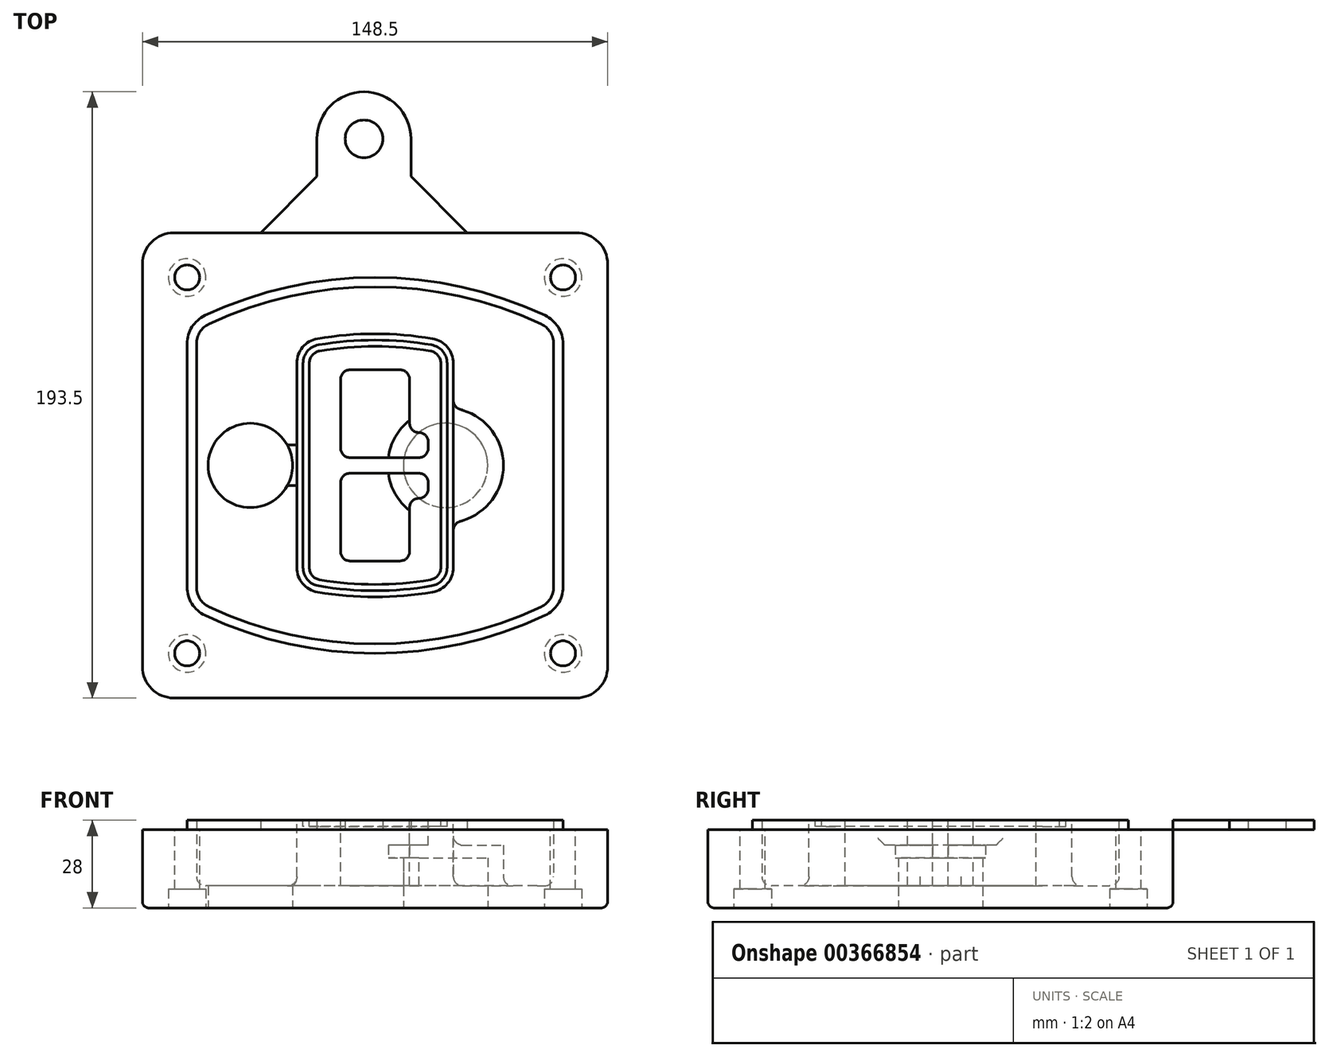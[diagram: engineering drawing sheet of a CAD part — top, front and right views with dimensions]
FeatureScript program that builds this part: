
annotation { "Feature Type Name" : "Feature", "Feature Type Description" : "" }
export const myFeature = defineFeature(function(context is Context, id is Id, definition is map)
    precondition{}
    {
        {
            var Q0;
            Q0=qCreatedBy(makeId("Top.planeOp"),FACE);
            var sketch = newSketch(context, id + "F0", { "sketchPlane" : qUnion([Q0])});
            skPoint(sketch, "E0.rect.middle", {"position": v(0, 0) * mm});
            skLineSegment(sketch, "E1.bottom", {"start": v(-64.25, -74.25) * mm, "end": v(64.25, -74.25) * mm});
            skLineSegment(sketch, "E1.top", {"start": v(-64.25, 74.25) * mm, "end": v(64.25, 74.25) * mm});
            skLineSegment(sketch, "E1.left", {"start": v(-74.25, -64.25) * mm, "end": v(-74.25, 64.25) * mm});
            skLineSegment(sketch, "E1.right", {"start": v(74.25, -64.25) * mm, "end": v(74.25, 64.25) * mm});
            skLineSegment(sketch, "E2", {"start": v(-74.25, 74.25) * mm, "end": v(74.25, -74.25) * mm, "construction": true});
            skLineSegment(sketch, "E3", {"start": v(74.25, 74.25) * mm, "end": v(-74.25, -74.25) * mm, "construction": true});
            skCircle(sketch, "E4", {"center": v(-60, 60) * mm, "radius": 4 * mm});
            skCircle(sketch, "E5", {"center": v(60, 60) * mm, "radius": 4 * mm});
            skCircle(sketch, "E6", {"center": v(60, -60) * mm, "radius": 4 * mm});
            skCircle(sketch, "E7", {"center": v(-60, -60) * mm, "radius": 4 * mm});
            skLineSegment(sketch, "E8", {"start": v(-60, 60) * mm, "end": v(60, 60) * mm, "construction": true});
            skLineSegment(sketch, "E9", {"start": v(60, 60) * mm, "end": v(60, -60) * mm, "construction": true});
            skLineSegment(sketch, "E10", {"start": v(60, -60) * mm, "end": v(-60, -60) * mm, "construction": true});
            skLineSegment(sketch, "E11", {"start": v(-60, -60) * mm, "end": v(-60, 60) * mm, "construction": true});
            skLineSegment(sketch, "E12", {"start": v(-60, 38.83) * mm, "end": v(-60, -38.83) * mm});
            skLineSegment(sketch, "E13", {"start": v(60, 38.83) * mm, "end": v(60, -38.83) * mm});
            skArc(sketch, "E14", {"start": v(54.26, 47.88) * mm, "mid": v(0, 60) * mm, "end": v(-54.26, 47.88) * mm});
            skArc(sketch, "E15", {"start": v(-54.26, -47.88) * mm, "mid": v(0, -60) * mm, "end": v(54.26, -47.88) * mm});
            skLineSegment(sketch, "E16", {"start": v(-60, 0) * mm, "end": v(60, 0) * mm, "construction": true});
            skPoint(sketch, "E17.visualSharp", {"position": v(-60, -45) * mm});
            skArc(sketch, "E17.filletArc", {"start": v(-60, -38.83) * mm, "mid": v(-58.44, -44.2) * mm, "end": v(-54.26, -47.88) * mm});
            skPoint(sketch, "E18.visualSharp", {"position": v(-60, 45) * mm});
            skArc(sketch, "E18.filletArc", {"start": v(-54.26, 47.88) * mm, "mid": v(-58.44, 44.2) * mm, "end": v(-60, 38.83) * mm});
            skPoint(sketch, "E19.visualSharp", {"position": v(60, 45) * mm});
            skArc(sketch, "E19.filletArc", {"start": v(60, 38.83) * mm, "mid": v(58.44, 44.2) * mm, "end": v(54.26, 47.88) * mm});
            skPoint(sketch, "E20.visualSharp", {"position": v(60, -45) * mm});
            skArc(sketch, "E20.filletArc", {"start": v(54.26, -47.88) * mm, "mid": v(58.44, -44.2) * mm, "end": v(60, -38.83) * mm});
            skPoint(sketch, "E21.visualSharp", {"position": v(-74.25, 74.25) * mm});
            skArc(sketch, "E21.filletArc", {"start": v(-64.25, 74.25) * mm, "mid": v(-71.32, 71.32) * mm, "end": v(-74.25, 64.25) * mm});
            skPoint(sketch, "E22.visualSharp", {"position": v(74.25, 74.25) * mm});
            skArc(sketch, "E22.filletArc", {"start": v(74.25, 64.25) * mm, "mid": v(71.32, 71.32) * mm, "end": v(64.25, 74.25) * mm});
            skPoint(sketch, "E23.visualSharp", {"position": v(74.25, -74.25) * mm});
            skArc(sketch, "E23.filletArc", {"start": v(64.25, -74.25) * mm, "mid": v(71.32, -71.32) * mm, "end": v(74.25, -64.25) * mm});
            skPoint(sketch, "E24.visualSharp", {"position": v(-74.25, -74.25) * mm});
            skArc(sketch, "E24.filletArc", {"start": v(-74.25, -64.25) * mm, "mid": v(-71.32, -71.32) * mm, "end": v(-64.25, -74.25) * mm});
            skArc(sketch, "E25.0", {"start": v(57, 38.83) * mm, "mid": v(55.9, 42.58) * mm, "end": v(52.98, 45.17) * mm});
            skLineSegment(sketch, "E25.1", {"start": v(57, 38.83) * mm, "end": v(57, -38.83) * mm});
            skArc(sketch, "E25.2", {"start": v(52.98, -45.17) * mm, "mid": v(55.9, -42.58) * mm, "end": v(57, -38.83) * mm});
            skArc(sketch, "E25.3", {"start": v(-52.98, -45.17) * mm, "mid": v(0, -57) * mm, "end": v(52.98, -45.17) * mm});
            skArc(sketch, "E25.4", {"start": v(-57, -38.83) * mm, "mid": v(-55.9, -42.58) * mm, "end": v(-52.98, -45.17) * mm});
            skArc(sketch, "E25.5", {"start": v(52.98, 45.17) * mm, "mid": v(0, 57) * mm, "end": v(-52.98, 45.17) * mm});
            skLineSegment(sketch, "E25.6", {"start": v(-57, 38.83) * mm, "end": v(-57, -38.83) * mm});
            skArc(sketch, "E25.7", {"start": v(-52.98, 45.17) * mm, "mid": v(-55.9, 42.58) * mm, "end": v(-57, 38.83) * mm});
            skArc(sketch, "E26.0", {"start": v(-55.96, 51.5) * mm, "mid": v(-61.82, 46.33) * mm, "end": v(-64, 38.83) * mm});
            skArc(sketch, "E26.1", {"start": v(55.96, 51.5) * mm, "mid": v(0, 64) * mm, "end": v(-55.96, 51.5) * mm});
            skArc(sketch, "E26.2", {"start": v(64, 38.83) * mm, "mid": v(61.82, 46.33) * mm, "end": v(55.96, 51.5) * mm});
            skLineSegment(sketch, "E26.3", {"start": v(64, 38.83) * mm, "end": v(64, -38.83) * mm});
            skArc(sketch, "E26.4", {"start": v(55.96, -51.5) * mm, "mid": v(61.82, -46.33) * mm, "end": v(64, -38.83) * mm});
            skLineSegment(sketch, "E26.5", {"start": v(-64, 38.83) * mm, "end": v(-64, -38.83) * mm});
            skArc(sketch, "E26.6", {"start": v(-55.96, -51.5) * mm, "mid": v(0, -64) * mm, "end": v(55.96, -51.5) * mm});
            skArc(sketch, "E26.7", {"start": v(-64, -38.83) * mm, "mid": v(-61.82, -46.33) * mm, "end": v(-55.96, -51.5) * mm});
            skSolve(sketch);
        }
        {
            var Q0;
            Q0=makeQuery(id+"F0.imprint","IMPRINT",FACE,{"disambiguationData":[TD([[makeQuery(id+"F0.imprint","IMPRINT",EDGE,{"derivedFrom":sQuery(id+"F0.wireOp",EDGE,"E1.bottom")}),1.0]])]});
            var Q1;
            Q1=makeQuery(id+"F0.imprint","IMPRINT",FACE,{"disambiguationData":[TD([[makeQuery(id+"F0.imprint","IMPRINT",EDGE,{"derivedFrom":sQuery(id+"F0.wireOp",EDGE,"E12")}),1.0]])]});
            var Q2;
            Q2=makeQuery(id+"F0.imprint","IMPRINT",FACE,{"disambiguationData":[TD([[makeQuery(id+"F0.imprint","IMPRINT",EDGE,{"derivedFrom":sQuery(id+"F0.wireOp",EDGE,"E25.0")}),1.0]])]});
            var Q3;
            Q3=makeQuery(id+"F0.imprint","IMPRINT",FACE,{"disambiguationData":[TD([[makeQuery(id+"F0.imprint","IMPRINT",EDGE,{"derivedFrom":sQuery(id+"F0.wireOp",EDGE,"E12")}),-1.0]])]});
            extrude(context, id + "F1", {"entities" : qUnion([Q0, Q1, Q2, Q3]), "oppositeDirection" : true, "depth" : 25 * mm});
        }
        {
            var Q0;
            Q0=makeQuery(id+"F0.imprint","IMPRINT",FACE,{"disambiguationData":[TD([[makeQuery(id+"F0.imprint","IMPRINT",EDGE,{"derivedFrom":sQuery(id+"F0.wireOp",EDGE,"E12")}),1.0]])]});
            extrude(context, id + "F2", {"entities" : qUnion([Q0]), "operationType" : NewBodyOperationType.ADD, "depth" : 3 * mm});
        }
        {
            var Q0;
            Q0=makeQuery(id+"F0.imprint","IMPRINT",FACE,{"disambiguationData":[TD([[makeQuery(id+"F0.imprint","IMPRINT",EDGE,{"derivedFrom":sQuery(id+"F0.wireOp",EDGE,"E25.0")}),1.0]])]});
            extrude(context, id + "F3", {"entities" : qUnion([Q0]), "operationType" : NewBodyOperationType.REMOVE, "oppositeDirection" : true, "depth" : 18 * mm});
        }
        {
            var Q0;
            Q0=makeQuery(id+"F2.opExtrude","CAP_FACE",FACE,{"disambiguationData":[OSD([sQuery(id+"F0.wireOp",EDGE,"E12"),sQuery(id+"F0.wireOp",EDGE,"E13"),sQuery(id+"F0.wireOp",EDGE,"E14"),sQuery(id+"F0.wireOp",EDGE,"E15"),sQuery(id+"F0.wireOp",EDGE,"E17.filletArc"),sQuery(id+"F0.wireOp",EDGE,"E18.filletArc"),sQuery(id+"F0.wireOp",EDGE,"E19.filletArc"),sQuery(id+"F0.wireOp",EDGE,"E20.filletArc"),sQuery(id+"F0.wireOp",EDGE,"E25.0"),sQuery(id+"F0.wireOp",EDGE,"E25.1"),sQuery(id+"F0.wireOp",EDGE,"E25.2"),sQuery(id+"F0.wireOp",EDGE,"E25.3"),sQuery(id+"F0.wireOp",EDGE,"E25.4"),sQuery(id+"F0.wireOp",EDGE,"E25.5"),sQuery(id+"F0.wireOp",EDGE,"E25.6"),sQuery(id+"F0.wireOp",EDGE,"E25.7")])],"isStart":false});
            var sketch = newSketch(context, id + "F4", { "sketchPlane" : qUnion([Q0])});
            skArc(sketch, "E27.0", {"start": v(-18.34, -40.45) * mm, "mid": v(0, -42) * mm, "end": v(18.34, -40.45) * mm});
            skArc(sketch, "E28.0", {"start": v(18.34, 40.45) * mm, "mid": v(0, 42) * mm, "end": v(-18.34, 40.45) * mm});
            skLineSegment(sketch, "E29", {"start": v(-25, 32.57) * mm, "end": v(-25, -32.57) * mm});
            skLineSegment(sketch, "E30", {"start": v(25, 32.57) * mm, "end": v(25, -32.57) * mm});
            skLineSegment(sketch, "E31", {"start": v(-25, 39.1) * mm, "end": v(25, 39.1) * mm, "construction": true});
            skLineSegment(sketch, "E32", {"start": v(-25, -39.1) * mm, "end": v(25, -39.1) * mm, "construction": true});
            skPoint(sketch, "E33.visualSharp", {"position": v(-25, 39.1) * mm});
            skArc(sketch, "E33.filletArc", {"start": v(-18.34, 40.45) * mm, "mid": v(-23.11, 37.73) * mm, "end": v(-25, 32.57) * mm});
            skPoint(sketch, "E34.visualSharp", {"position": v(25, 39.1) * mm});
            skArc(sketch, "E34.filletArc", {"start": v(25, 32.57) * mm, "mid": v(23.11, 37.73) * mm, "end": v(18.34, 40.45) * mm});
            skPoint(sketch, "E35.visualSharp", {"position": v(25, -39.1) * mm});
            skArc(sketch, "E35.filletArc", {"start": v(18.34, -40.45) * mm, "mid": v(23.11, -37.73) * mm, "end": v(25, -32.57) * mm});
            skPoint(sketch, "E36.visualSharp", {"position": v(-25, -39.1) * mm});
            skArc(sketch, "E36.filletArc", {"start": v(-25, -32.57) * mm, "mid": v(-23.11, -37.73) * mm, "end": v(-18.34, -40.45) * mm});
            skArc(sketch, "E37.0", {"start": v(52.98, 45.17) * mm, "mid": v(0, 57) * mm, "end": v(-52.98, 45.17) * mm});
            skArc(sketch, "E37.1", {"start": v(-52.98, 45.17) * mm, "mid": v(-55.9, 42.58) * mm, "end": v(-57, 38.83) * mm});
            skLineSegment(sketch, "E37.2", {"start": v(-57, 38.83) * mm, "end": v(-57, -38.83) * mm});
            skArc(sketch, "E37.3", {"start": v(-57, -38.83) * mm, "mid": v(-55.9, -42.58) * mm, "end": v(-52.98, -45.17) * mm});
            skArc(sketch, "E37.4", {"start": v(-52.98, -45.17) * mm, "mid": v(0, -57) * mm, "end": v(52.98, -45.17) * mm});
            skArc(sketch, "E37.5", {"start": v(52.98, -45.17) * mm, "mid": v(55.9, -42.58) * mm, "end": v(57, -38.83) * mm});
            skLineSegment(sketch, "E37.6", {"start": v(57, 38.83) * mm, "end": v(57, -38.83) * mm});
            skArc(sketch, "E37.7", {"start": v(57, 38.83) * mm, "mid": v(55.9, 42.58) * mm, "end": v(52.98, 45.17) * mm});
            skLineSegment(sketch, "E38.0", {"start": v(23, 32.57) * mm, "end": v(23, -32.57) * mm});
            skArc(sketch, "E38.1", {"start": v(18, -38.48) * mm, "mid": v(21.58, -36.44) * mm, "end": v(23, -32.57) * mm});
            skArc(sketch, "E38.2", {"start": v(-18, -38.48) * mm, "mid": v(0, -40) * mm, "end": v(18, -38.48) * mm});
            skArc(sketch, "E38.3", {"start": v(-23, -32.57) * mm, "mid": v(-21.58, -36.44) * mm, "end": v(-18, -38.48) * mm});
            skLineSegment(sketch, "E38.4", {"start": v(-23, 32.57) * mm, "end": v(-23, -32.57) * mm});
            skArc(sketch, "E38.5", {"start": v(23, 32.57) * mm, "mid": v(21.58, 36.44) * mm, "end": v(18, 38.48) * mm});
            skArc(sketch, "E38.6", {"start": v(-18, 38.48) * mm, "mid": v(-21.58, 36.44) * mm, "end": v(-23, 32.57) * mm});
            skArc(sketch, "E38.7", {"start": v(18, 38.48) * mm, "mid": v(0, 40) * mm, "end": v(-18, 38.48) * mm});
            skArc(sketch, "E39.0", {"start": v(21, 32.57) * mm, "mid": v(20.06, 35.15) * mm, "end": v(17.67, 36.5) * mm});
            skLineSegment(sketch, "E39.1", {"start": v(21, 32.57) * mm, "end": v(21, -32.57) * mm});
            skArc(sketch, "E39.2", {"start": v(17.67, -36.5) * mm, "mid": v(20.06, -35.15) * mm, "end": v(21, -32.57) * mm});
            skArc(sketch, "E39.3", {"start": v(-17.67, -36.5) * mm, "mid": v(0, -38) * mm, "end": v(17.67, -36.5) * mm});
            skArc(sketch, "E39.4", {"start": v(-21, -32.57) * mm, "mid": v(-20.06, -35.15) * mm, "end": v(-17.67, -36.5) * mm});
            skArc(sketch, "E39.5", {"start": v(17.67, 36.5) * mm, "mid": v(0, 38) * mm, "end": v(-17.67, 36.5) * mm});
            skLineSegment(sketch, "E39.6", {"start": v(-21, 32.57) * mm, "end": v(-21, -32.57) * mm});
            skArc(sketch, "E39.7", {"start": v(-17.67, 36.5) * mm, "mid": v(-20.06, 35.15) * mm, "end": v(-21, 32.57) * mm});
            skLineSegment(sketch, "E40", {"start": v(-25, 0) * mm, "end": v(25, 0) * mm, "construction": true});
            skLineSegment(sketch, "E41", {"start": v(-11, 5.5) * mm, "end": v(-11, 27.5) * mm});
            skLineSegment(sketch, "E42", {"start": v(-8, 30.5) * mm, "end": v(8, 30.5) * mm});
            skLineSegment(sketch, "E43", {"start": v(11, 27.5) * mm, "end": v(11, 13.5) * mm});
            skLineSegment(sketch, "E44", {"start": v(14, 10.5) * mm, "end": v(14, 10.5) * mm});
            skLineSegment(sketch, "E45", {"start": v(17, 7.5) * mm, "end": v(17, 5.5) * mm});
            skLineSegment(sketch, "E46", {"start": v(14, 2.5) * mm, "end": v(-8, 2.5) * mm});
            skPoint(sketch, "E47.visualSharp", {"position": v(-11, 30.5) * mm});
            skArc(sketch, "E47.filletArc", {"start": v(-8, 30.5) * mm, "mid": v(-10.12, 29.62) * mm, "end": v(-11, 27.5) * mm});
            skPoint(sketch, "E48.visualSharp", {"position": v(11, 30.5) * mm});
            skArc(sketch, "E48.filletArc", {"start": v(11, 27.5) * mm, "mid": v(10.12, 29.62) * mm, "end": v(8, 30.5) * mm});
            skPoint(sketch, "E49.visualSharp", {"position": v(11, 10.5) * mm});
            skArc(sketch, "E49.filletArc", {"start": v(11, 13.5) * mm, "mid": v(11.88, 11.38) * mm, "end": v(14, 10.5) * mm});
            skPoint(sketch, "E50.visualSharp", {"position": v(17, 10.5) * mm});
            skArc(sketch, "E50.filletArc", {"start": v(17, 7.5) * mm, "mid": v(16.12, 9.62) * mm, "end": v(14, 10.5) * mm});
            skPoint(sketch, "E51.visualSharp", {"position": v(17, 2.5) * mm});
            skArc(sketch, "E51.filletArc", {"start": v(14, 2.5) * mm, "mid": v(16.12, 3.38) * mm, "end": v(17, 5.5) * mm});
            skPoint(sketch, "E52.visualSharp", {"position": v(-11, 2.5) * mm});
            skArc(sketch, "E52.filletArc", {"start": v(-11, 5.5) * mm, "mid": v(-10.12, 3.38) * mm, "end": v(-8, 2.5) * mm});
            skLineSegment(sketch, "E53.0.MirrorCS", {"start": v(14, -2.5) * mm, "end": v(-8, -2.5) * mm});
            skArc(sketch, "E54.0.MirrorCS", {"start": v(-11, -5.5) * mm, "mid": v(-10.12, -3.38) * mm, "end": v(-8, -2.5) * mm});
            skLineSegment(sketch, "E55.0.MirrorCS", {"start": v(-11, -5.5) * mm, "end": v(-11, -27.5) * mm});
            skArc(sketch, "E56.0.MirrorCS", {"start": v(-8, -30.5) * mm, "mid": v(-10.12, -29.62) * mm, "end": v(-11, -27.5) * mm});
            skLineSegment(sketch, "E57.0.MirrorCS", {"start": v(-8, -30.5) * mm, "end": v(8, -30.5) * mm});
            skArc(sketch, "E58.0.MirrorCS", {"start": v(11, -27.5) * mm, "mid": v(10.12, -29.62) * mm, "end": v(8, -30.5) * mm});
            skLineSegment(sketch, "E59.0.MirrorCS", {"start": v(11, -27.5) * mm, "end": v(11, -13.5) * mm});
            skArc(sketch, "E60.0.MirrorCS", {"start": v(11, -13.5) * mm, "mid": v(11.88, -11.38) * mm, "end": v(14, -10.5) * mm});
            skArc(sketch, "E61.0.MirrorCS", {"start": v(17, -7.5) * mm, "mid": v(16.12, -9.62) * mm, "end": v(14, -10.5) * mm});
            skLineSegment(sketch, "E62.0.MirrorCS", {"start": v(17, -7.5) * mm, "end": v(17, -5.5) * mm});
            skArc(sketch, "E63.0.MirrorCS", {"start": v(14, -2.5) * mm, "mid": v(16.12, -3.38) * mm, "end": v(17, -5.5) * mm});
            skSolve(sketch);
        }
        {
            var Q0;
            Q0=makeQuery(id+"F4.imprint","IMPRINT",FACE,{"disambiguationData":[TD([[makeQuery(id+"F4.imprint","IMPRINT",EDGE,{"derivedFrom":sQuery(id+"F4.wireOp",EDGE,"E27.0")}),1.0]])]});
            var Q1;
            Q1=makeQuery(id+"F4.imprint","IMPRINT",FACE,{"disambiguationData":[TD([[makeQuery(id+"F4.imprint","IMPRINT",EDGE,{"derivedFrom":sQuery(id+"F4.wireOp",EDGE,"E38.0")}),-1.0]])]});
            var Q2;
            Q2=makeQuery(id+"F4.imprint","IMPRINT",FACE,{"disambiguationData":[TD([[makeQuery(id+"F4.imprint","IMPRINT",EDGE,{"derivedFrom":sQuery(id+"F4.wireOp",EDGE,"E39.0")}),1.0]])]});
            extrude(context, id + "F5", {"entities" : qUnion([Q0, Q1, Q2]), "operationType" : NewBodyOperationType.ADD, "endBound" : BoundingType.UP_TO_NEXT, "oppositeDirection" : true, "depth" : 25 * mm});
        }
        {
            var Q0;
            Q0=makeQuery(id+"F4.imprint","IMPRINT",FACE,{"disambiguationData":[TD([[makeQuery(id+"F4.imprint","IMPRINT",EDGE,{"derivedFrom":sQuery(id+"F4.wireOp",EDGE,"E38.0")}),-1.0]])]});
            extrude(context, id + "F6", {"entities" : qUnion([Q0]), "operationType" : NewBodyOperationType.REMOVE, "oppositeDirection" : true, "depth" : 2 * mm});
        }
        {
            var Q0;
            Q0=makeQuery(id+"F1.opExtrude","CAP_FACE",FACE,{"disambiguationData":[OSD([sQuery(id+"F0.wireOp",EDGE,"E1.bottom"),sQuery(id+"F0.wireOp",EDGE,"E1.top"),sQuery(id+"F0.wireOp",EDGE,"E1.left"),sQuery(id+"F0.wireOp",EDGE,"E1.right"),sQuery(id+"F0.wireOp",EDGE,"E4"),sQuery(id+"F0.wireOp",EDGE,"E5"),sQuery(id+"F0.wireOp",EDGE,"E6"),sQuery(id+"F0.wireOp",EDGE,"E7"),sQuery(id+"F0.wireOp",EDGE,"E21.filletArc"),sQuery(id+"F0.wireOp",EDGE,"E22.filletArc"),sQuery(id+"F0.wireOp",EDGE,"E23.filletArc"),sQuery(id+"F0.wireOp",EDGE,"E24.filletArc")])],"isStart":false});
            var sketch = newSketch(context, id + "F7", { "sketchPlane" : qUnion([Q0])});
            skCircle(sketch, "E64", {"center": v(22.5, 0) * mm, "radius": 13.47 * mm});
            skCircle(sketch, "E65", {"center": v(-39.81, 0) * mm, "radius": 13.47 * mm});
            skLineSegment(sketch, "E66", {"start": v(74.25, 0) * mm, "end": v(-74.25, 0) * mm});
            skCircle(sketch, "E67", {"center": v(22.5, 0) * mm, "radius": 18.47 * mm});
            skCircle(sketch, "E68", {"center": v(60, -60) * mm, "radius": 6 * mm});
            skCircle(sketch, "E69", {"center": v(-60, -60) * mm, "radius": 6 * mm});
            skCircle(sketch, "E70", {"center": v(-60, 60) * mm, "radius": 6 * mm});
            skCircle(sketch, "E71", {"center": v(60, 60) * mm, "radius": 6 * mm});
            skSolve(sketch);
        }
        {
            var Q0;
            {var subQ1=sQuery(id+"F7.wireOp",EDGE,"E66");var subQ4=sQuery(id+"F7.wireOp",EDGE,"E64");var subQ6=makeQuery(id+"F7.imprint","INTERSECT",VERTEX,{"disambiguationData":[OD(0.0)],"derivedFrom":[subQ4,subQ1]});Q0=makeQuery(id+"F7.imprint","IMPRINT",FACE,{"disambiguationData":[TD([[makeQuery(id+"F7.imprint","IMPRINT",EDGE,{"disambiguationData":[TD([[subQ6,-1.0]])],"derivedFrom":subQ4}),-1.0]])]});}
            var Q1;
            {var subQ0=sQuery(id+"F7.wireOp",EDGE,"E66");var subQ1=sQuery(id+"F7.wireOp",EDGE,"E64");var subQ3=makeQuery(id+"F7.imprint","INTERSECT",VERTEX,{"disambiguationData":[OD(0.0)],"derivedFrom":[subQ1,subQ0]});Q1=makeQuery(id+"F7.imprint","IMPRINT",FACE,{"disambiguationData":[TD([[makeQuery(id+"F7.imprint","IMPRINT",EDGE,{"disambiguationData":[TD([[subQ3,-1.0]])],"derivedFrom":subQ1}),1.0]])]});}
            var Q2;
            {var subQ0=sQuery(id+"F7.wireOp",EDGE,"E66");var subQ1=sQuery(id+"F7.wireOp",EDGE,"E64");var subQ3=makeQuery(id+"F7.imprint","INTERSECT",VERTEX,{"disambiguationData":[OD(0.0)],"derivedFrom":[subQ1,subQ0]});Q2=makeQuery(id+"F7.imprint","IMPRINT",FACE,{"disambiguationData":[TD([[makeQuery(id+"F7.imprint","IMPRINT",EDGE,{"disambiguationData":[TD([[subQ3,1.0]])],"derivedFrom":subQ1}),1.0]])]});}
            var Q3;
            {var subQ1=sQuery(id+"F7.wireOp",EDGE,"E66");var subQ4=sQuery(id+"F7.wireOp",EDGE,"E64");var subQ6=makeQuery(id+"F7.imprint","INTERSECT",VERTEX,{"disambiguationData":[OD(0.0)],"derivedFrom":[subQ4,subQ1]});Q3=makeQuery(id+"F7.imprint","IMPRINT",FACE,{"disambiguationData":[TD([[makeQuery(id+"F7.imprint","IMPRINT",EDGE,{"disambiguationData":[TD([[subQ6,1.0]])],"derivedFrom":subQ4}),-1.0]])]});}
            extrude(context, id + "F8", {"entities" : qUnion([Q0, Q1, Q2, Q3]), "operationType" : NewBodyOperationType.ADD, "oppositeDirection" : true, "depth" : 20 * mm});
        }
        {
            var Q0;
            {var subQ0=sQuery(id+"F7.wireOp",EDGE,"E66");var subQ1=sQuery(id+"F7.wireOp",EDGE,"E64");var subQ3=makeQuery(id+"F7.imprint","INTERSECT",VERTEX,{"disambiguationData":[OD(0.0)],"derivedFrom":[subQ1,subQ0]});Q0=makeQuery(id+"F7.imprint","IMPRINT",FACE,{"disambiguationData":[TD([[makeQuery(id+"F7.imprint","IMPRINT",EDGE,{"disambiguationData":[TD([[subQ3,-1.0]])],"derivedFrom":subQ1}),1.0]])]});}
            var Q1;
            {var subQ0=sQuery(id+"F7.wireOp",EDGE,"E66");var subQ1=sQuery(id+"F7.wireOp",EDGE,"E64");var subQ3=makeQuery(id+"F7.imprint","INTERSECT",VERTEX,{"disambiguationData":[OD(0.0)],"derivedFrom":[subQ1,subQ0]});Q1=makeQuery(id+"F7.imprint","IMPRINT",FACE,{"disambiguationData":[TD([[makeQuery(id+"F7.imprint","IMPRINT",EDGE,{"disambiguationData":[TD([[subQ3,1.0]])],"derivedFrom":subQ1}),1.0]])]});}
            extrude(context, id + "F9", {"entities" : qUnion([Q0, Q1]), "operationType" : NewBodyOperationType.REMOVE, "oppositeDirection" : true, "depth" : 16 * mm});
        }
        {
            var Q0;
            {var subQ0=sQuery(id+"F7.wireOp",EDGE,"E66");var subQ1=sQuery(id+"F7.wireOp",EDGE,"E65");var subQ3=makeQuery(id+"F7.imprint","INTERSECT",VERTEX,{"disambiguationData":[OD(0.0)],"derivedFrom":[subQ1,subQ0]});Q0=makeQuery(id+"F7.imprint","IMPRINT",FACE,{"disambiguationData":[TD([[makeQuery(id+"F7.imprint","IMPRINT",EDGE,{"disambiguationData":[TD([[subQ3,-1.0]])],"derivedFrom":subQ1}),1.0]])]});}
            var Q1;
            {var subQ0=sQuery(id+"F7.wireOp",EDGE,"E66");var subQ1=sQuery(id+"F7.wireOp",EDGE,"E65");var subQ3=makeQuery(id+"F7.imprint","INTERSECT",VERTEX,{"disambiguationData":[OD(0.0)],"derivedFrom":[subQ1,subQ0]});Q1=makeQuery(id+"F7.imprint","IMPRINT",FACE,{"disambiguationData":[TD([[makeQuery(id+"F7.imprint","IMPRINT",EDGE,{"disambiguationData":[TD([[subQ3,1.0]])],"derivedFrom":subQ1}),1.0]])]});}
            extrude(context, id + "F10", {"entities" : qUnion([Q0, Q1]), "operationType" : NewBodyOperationType.REMOVE, "oppositeDirection" : true, "depth" : 25 * mm});
        }
        {
            var Q0;
            Q0=makeQuery(id+"F7.imprint","IMPRINT",FACE,{"disambiguationData":[TD([[makeQuery(id+"F7.imprint","IMPRINT",EDGE,{"derivedFrom":sQuery(id+"F7.wireOp",EDGE,"E68")}),1.0]])]});
            var Q1;
            Q1=makeQuery(id+"F7.imprint","IMPRINT",FACE,{"disambiguationData":[TD([[makeQuery(id+"F7.imprint","IMPRINT",EDGE,{"derivedFrom":makeQuery(id+"F1.opExtrude","CAP_EDGE",EDGE,{"disambiguationData":[OSD([sQuery(id+"F0.wireOp",EDGE,"E5")])],"isStart":false})}),-1.0]])]});
            var Q2;
            Q2=makeQuery(id+"F7.imprint","IMPRINT",FACE,{"disambiguationData":[TD([[makeQuery(id+"F7.imprint","IMPRINT",EDGE,{"derivedFrom":sQuery(id+"F7.wireOp",EDGE,"E69")}),1.0]])]});
            var Q3;
            Q3=makeQuery(id+"F7.imprint","IMPRINT",FACE,{"disambiguationData":[TD([[makeQuery(id+"F7.imprint","IMPRINT",EDGE,{"derivedFrom":makeQuery(id+"F1.opExtrude","CAP_EDGE",EDGE,{"disambiguationData":[OSD([sQuery(id+"F0.wireOp",EDGE,"E4")])],"isStart":false})}),-1.0]])]});
            var Q4;
            Q4=makeQuery(id+"F7.imprint","IMPRINT",FACE,{"disambiguationData":[TD([[makeQuery(id+"F7.imprint","IMPRINT",EDGE,{"derivedFrom":sQuery(id+"F7.wireOp",EDGE,"E70")}),1.0]])]});
            var Q5;
            Q5=makeQuery(id+"F7.imprint","IMPRINT",FACE,{"disambiguationData":[TD([[makeQuery(id+"F7.imprint","IMPRINT",EDGE,{"derivedFrom":makeQuery(id+"F1.opExtrude","CAP_EDGE",EDGE,{"disambiguationData":[OSD([sQuery(id+"F0.wireOp",EDGE,"E7")])],"isStart":false})}),-1.0]])]});
            var Q6;
            Q6=makeQuery(id+"F7.imprint","IMPRINT",FACE,{"disambiguationData":[TD([[makeQuery(id+"F7.imprint","IMPRINT",EDGE,{"derivedFrom":sQuery(id+"F7.wireOp",EDGE,"E71")}),1.0]])]});
            var Q7;
            Q7=makeQuery(id+"F7.imprint","IMPRINT",FACE,{"disambiguationData":[TD([[makeQuery(id+"F7.imprint","IMPRINT",EDGE,{"derivedFrom":makeQuery(id+"F1.opExtrude","CAP_EDGE",EDGE,{"disambiguationData":[OSD([sQuery(id+"F0.wireOp",EDGE,"E6")])],"isStart":false})}),-1.0]])]});
            extrude(context, id + "F11", {"entities" : qUnion([Q0, Q1, Q2, Q3, Q4, Q5, Q6, Q7]), "operationType" : NewBodyOperationType.REMOVE, "oppositeDirection" : true, "depth" : 6 * mm});
        }
        {
            var Q0;
            Q0=makeQuery(id+"F9.boolean.opBoolean","COPY",FACE,{"derivedFrom":makeQuery(id+"F9.opExtrude","CAP_FACE",FACE,{"disambiguationData":[OSD([sQuery(id+"F7.wireOp",EDGE,"E64")])],"isStart":false})});
            var sketch = newSketch(context, id + "F12", { "sketchPlane" : qUnion([Q0])});
            skArc(sketch, "E72.0", {"start": v(11, 14.45) * mm, "mid": v(6.45, 9.13) * mm, "end": v(4.2, 2.5) * mm});
            skArc(sketch, "E72.1", {"start": v(4.2, -2.5) * mm, "mid": v(6.45, -9.13) * mm, "end": v(11, -14.45) * mm});
            skLineSegment(sketch, "E73", {"start": v(4.2, -2.5) * mm, "end": v(14, -2.5) * mm});
            skLineSegment(sketch, "E74.0", {"start": v(14, 2.5) * mm, "end": v(4.2, 2.5) * mm});
            skArc(sketch, "E74.1", {"start": v(14, 2.5) * mm, "mid": v(16.12, 3.38) * mm, "end": v(17, 5.5) * mm});
            skLineSegment(sketch, "E74.2", {"start": v(17, 7.5) * mm, "end": v(17, 5.5) * mm});
            skArc(sketch, "E74.3", {"start": v(17, 7.5) * mm, "mid": v(16.12, 9.62) * mm, "end": v(14, 10.5) * mm});
            skArc(sketch, "E74.4", {"start": v(11, 13.5) * mm, "mid": v(11.88, 11.38) * mm, "end": v(14, 10.5) * mm});
            skLineSegment(sketch, "E74.5", {"start": v(11, 14.45) * mm, "end": v(11, 13.5) * mm});
            skLineSegment(sketch, "E74.7", {"start": v(14, -2.5) * mm, "end": v(4.2, -2.5) * mm});
            skArc(sketch, "E74.8", {"start": v(14, -2.5) * mm, "mid": v(16.12, -3.38) * mm, "end": v(17, -5.5) * mm});
            skLineSegment(sketch, "E74.9", {"start": v(17, -7.5) * mm, "end": v(17, -5.5) * mm});
            skArc(sketch, "E74.10", {"start": v(17, -7.5) * mm, "mid": v(16.12, -9.62) * mm, "end": v(14, -10.5) * mm});
            skArc(sketch, "E74.11", {"start": v(11, -13.5) * mm, "mid": v(11.88, -11.38) * mm, "end": v(14, -10.5) * mm});
            skLineSegment(sketch, "E74.12", {"start": v(11, -14.45) * mm, "end": v(11, -13.5) * mm});
            skPoint(sketch, "E75.orphan", {"position": v(11, -27.5) * mm});
            skPoint(sketch, "E76.orphan", {"position": v(-8, -2.5) * mm});
            skPoint(sketch, "E77.orphan", {"position": v(-8, 2.5) * mm});
            skPoint(sketch, "E78.orphan", {"position": v(11, 27.5) * mm});
            skSolve(sketch);
        }
        {
            var Q0;
            {var subQ7=sQuery(id+"F12.wireOp",EDGE,"E72.0");var subQ14=sQuery(id+"F12.wireOp",EDGE,"E72.1");var subQ16=sQuery(id+"F12.wireOp",EDGE,"E74.1");var subQ18=sQuery(id+"F12.wireOp",EDGE,"E74.8");Q0=qUnion([makeQuery(id+"F12.imprint","IMPRINT",FACE,{"disambiguationData":[TD([[makeQuery(id+"F12.imprint","IMPRINT",EDGE,{"derivedFrom":subQ7}),1.0]])]}),makeQuery(id+"F12.imprint","IMPRINT",FACE,{"disambiguationData":[TD([[makeQuery(id+"F12.imprint","IMPRINT",EDGE,{"derivedFrom":subQ14}),1.0]])]}),makeQuery(id+"F12.imprint","IMPRINT",FACE,{"disambiguationData":[TD([[makeQuery(id+"F12.imprint","IMPRINT",EDGE,{"derivedFrom":subQ16}),1.0]])]}),makeQuery(id+"F12.imprint","IMPRINT",FACE,{"disambiguationData":[TD([[makeQuery(id+"F12.imprint","IMPRINT",EDGE,{"derivedFrom":subQ18}),-1.0]])]})]);}
            var Q1;
            Q1=makeQuery(id+"F5.boolean.opBoolean","SPLIT",FACE,{"disambiguationData":[TD([makeQuery(id+"F5.opExtrude","SWEPT_FACE",FACE,{"disambiguationData":[OSD([sQuery(id+"F4.wireOp",EDGE,"E41")])]})])],"derivedFrom":makeQuery(id+"F3.boolean.opBoolean","COPY",FACE,{"derivedFrom":makeQuery(id+"F3.opExtrude","CAP_FACE",FACE,{"disambiguationData":[OSD([sQuery(id+"F0.wireOp",EDGE,"E25.0"),sQuery(id+"F0.wireOp",EDGE,"E25.1"),sQuery(id+"F0.wireOp",EDGE,"E25.2"),sQuery(id+"F0.wireOp",EDGE,"E25.3"),sQuery(id+"F0.wireOp",EDGE,"E25.4"),sQuery(id+"F0.wireOp",EDGE,"E25.5"),sQuery(id+"F0.wireOp",EDGE,"E25.6"),sQuery(id+"F0.wireOp",EDGE,"E25.7")])],"isStart":false})})});
            extrude(context, id + "F13", {"entities" : qUnion([Q0]), "operationType" : NewBodyOperationType.REMOVE, "endBound" : BoundingType.UP_TO_SURFACE, "endBoundEntityFace" : qUnion([Q1]), "depth" : 25 * mm});
        }
        {
            var Q0;
            Q0=makeQuery(id+"F3.boolean.opBoolean","COPY",EDGE,{"derivedFrom":makeQuery(id+"F3.opExtrude","CAP_EDGE",EDGE,{"disambiguationData":[OSD([sQuery(id+"F0.wireOp",EDGE,"E25.6")])],"isStart":false})});
            var Q1;
            Q1=makeQuery(id+"F8.boolean.opBoolean","INTERSECT",EDGE,{"derivedFrom":[makeQuery(id+"F5.opExtrude","SWEPT_FACE",FACE,{"disambiguationData":[OSD([sQuery(id+"F4.wireOp",EDGE,"E30")])]}),makeQuery(id+"F8.opExtrude","CAP_FACE",FACE,{"disambiguationData":[OSD([sQuery(id+"F7.wireOp",EDGE,"E67")])],"isStart":false})]});
            var Q2;
            Q2=makeQuery(id+"F8.boolean.opBoolean","INTERSECT",EDGE,{"disambiguationData":[OD(1.0)],"derivedFrom":[makeQuery(id+"F5.opExtrude","SWEPT_FACE",FACE,{"disambiguationData":[OSD([sQuery(id+"F4.wireOp",EDGE,"E30")])]}),makeQuery(id+"F8.opExtrude","SWEPT_FACE",FACE,{"disambiguationData":[OSD([sQuery(id+"F7.wireOp",EDGE,"E67")])]})]});
            var Q3;
            {var subQ0=sQuery(id+"F4.wireOp",EDGE,"E30");Q3=makeQuery(id+"F8.boolean.opBoolean","SPLIT",EDGE,{"disambiguationData":[TD([makeQuery(id+"F5.opExtrude","SWEPT_FACE",FACE,{"disambiguationData":[OSD([sQuery(id+"F4.wireOp",EDGE,"E35.filletArc")])]})])],"derivedFrom":makeQuery(id+"F5.opExtrude","CAP_EDGE",EDGE,{"disambiguationData":[OSD([subQ0])],"isStart":false})});}
            var Q4;
            {var subQ0=sQuery(id+"F0.wireOp",EDGE,"E25.7");var subQ1=sQuery(id+"F0.wireOp",EDGE,"E25.1");var subQ2=sQuery(id+"F0.wireOp",EDGE,"E25.6");var subQ3=sQuery(id+"F0.wireOp",EDGE,"E25.5");var subQ4=sQuery(id+"F0.wireOp",EDGE,"E25.4");var subQ5=sQuery(id+"F0.wireOp",EDGE,"E25.0");var subQ6=sQuery(id+"F0.wireOp",EDGE,"E25.2");var subQ7=sQuery(id+"F0.wireOp",EDGE,"E25.3");Q4=makeQuery(id+"F8.boolean.opBoolean","INTERSECT",EDGE,{"derivedFrom":[makeQuery(id+"F5.boolean.opBoolean","SPLIT",FACE,{"disambiguationData":[TD([makeQuery(id+"F2.opExtrude","SWEPT_FACE",FACE,{"disambiguationData":[OSD([subQ5])]})])],"derivedFrom":makeQuery(id+"F3.boolean.opBoolean","COPY",FACE,{"derivedFrom":makeQuery(id+"F3.opExtrude","CAP_FACE",FACE,{"disambiguationData":[OSD([subQ5,subQ1,subQ6,subQ7,subQ4,subQ3,subQ2,subQ0])],"isStart":false})})}),makeQuery(id+"F8.opExtrude","SWEPT_FACE",FACE,{"disambiguationData":[OSD([sQuery(id+"F7.wireOp",EDGE,"E67")])]})]});}
            var Q5;
            Q5=makeQuery(id+"F8.boolean.opBoolean","INTERSECT",EDGE,{"disambiguationData":[OD(0.0)],"derivedFrom":[makeQuery(id+"F5.opExtrude","SWEPT_FACE",FACE,{"disambiguationData":[OSD([sQuery(id+"F4.wireOp",EDGE,"E30")])]}),makeQuery(id+"F8.opExtrude","SWEPT_FACE",FACE,{"disambiguationData":[OSD([sQuery(id+"F7.wireOp",EDGE,"E67")])]})]});
            fillet(context, id + "F14", {"entities" : qUnion([Q0, Q1, Q2, Q3, Q4, Q5]), "radius" : 3 * mm, "tangentPropagation" : true, "allowEdgeOverflow" : false});
        }
        {
            var Q0;
            Q0=makeQuery(id+"F1.opExtrude","CAP_EDGE",EDGE,{"disambiguationData":[OSD([sQuery(id+"F0.wireOp",EDGE,"E1.bottom")])],"isStart":false});
            fillet(context, id + "F15", {"entities" : qUnion([Q0]), "radius" : 2 * mm, "tangentPropagation" : true, "allowEdgeOverflow" : false});
        }
        {
            var Q0;
            {var subQ0=sQuery(id+"F0.wireOp",EDGE,"E21.filletArc");var subQ1=sQuery(id+"F0.wireOp",EDGE,"E7");var subQ2=sQuery(id+"F0.wireOp",EDGE,"E6");var subQ3=sQuery(id+"F0.wireOp",EDGE,"E5");var subQ4=sQuery(id+"F0.wireOp",EDGE,"E4");var subQ5=sQuery(id+"F0.wireOp",EDGE,"E22.filletArc");var subQ6=sQuery(id+"F0.wireOp",EDGE,"E1.bottom");var subQ7=sQuery(id+"F0.wireOp",EDGE,"E1.right");var subQ8=sQuery(id+"F0.wireOp",EDGE,"E1.top");var subQ9=sQuery(id+"F0.wireOp",EDGE,"E1.left");var subQ10=sQuery(id+"F0.wireOp",EDGE,"E23.filletArc");var subQ11=sQuery(id+"F0.wireOp",EDGE,"E24.filletArc");Q0=makeQuery(id+"F2.boolean.opBoolean","SPLIT",FACE,{"disambiguationData":[TD([makeQuery(id+"F1.opExtrude","SWEPT_FACE",FACE,{"disambiguationData":[OSD([subQ6])]})])],"derivedFrom":makeQuery(id+"F1.opExtrude","CAP_FACE",FACE,{"disambiguationData":[OSD([subQ6,subQ8,subQ9,subQ7,subQ4,subQ3,subQ2,subQ1,subQ0,subQ5,subQ10,subQ11])],"isStart":true})});}
            var sketch = newSketch(context, id + "F16", { "sketchPlane" : qUnion([Q0])});
            skLineSegment(sketch, "E79", {"start": v(-36.54, 74.25) * mm, "end": v(-18.54, 92.25) * mm});
            skLineSegment(sketch, "E80", {"start": v(-18.54, 92.25) * mm, "end": v(-18.54, 104.25) * mm});
            skLineSegment(sketch, "E81", {"start": v(29.46, 74.25) * mm, "end": v(11.46, 92.25) * mm});
            skLineSegment(sketch, "E82", {"start": v(11.46, 92.25) * mm, "end": v(11.46, 104.25) * mm});
            skArc(sketch, "E83", {"start": v(11.46, 104.25) * mm, "mid": v(-3.54, 119.25) * mm, "end": v(-18.54, 104.25) * mm});
            skCircle(sketch, "E84", {"center": v(-3.54, 104.25) * mm, "radius": 6 * mm});
            skLineSegment(sketch, "E85", {"start": v(-3.54, 104.25) * mm, "end": v(-3.54, 74.25) * mm, "construction": true});
            skLineSegment(sketch, "E86", {"start": v(-74.25, 0) * mm, "end": v(74.25, 0) * mm, "construction": true});
            skArc(sketch, "E87.MirrorCS", {"start": v(11.46, -104.25) * mm, "mid": v(-3.54, -119.25) * mm, "end": v(-18.54, -104.25) * mm});
            skLineSegment(sketch, "E88.MirrorCS", {"start": v(-18.54, -92.25) * mm, "end": v(-18.54, -104.25) * mm});
            skLineSegment(sketch, "E89.MirrorCS", {"start": v(-36.54, -74.25) * mm, "end": v(-18.54, -92.25) * mm});
            skLineSegment(sketch, "E90.MirrorCS", {"start": v(29.46, -74.25) * mm, "end": v(11.46, -92.25) * mm});
            skLineSegment(sketch, "E91.MirrorCS", {"start": v(11.46, -92.25) * mm, "end": v(11.46, -104.25) * mm});
            skCircle(sketch, "E92.MirrorC", {"center": v(-3.54, -104.25) * mm, "radius": 6 * mm});
            skLineSegment(sketch, "E93.MirrorCS", {"start": v(-3.54, -104.25) * mm, "end": v(-3.54, -74.25) * mm, "construction": true});
            skSolve(sketch);
        }
        {
            var Q0;
            Q0=makeQuery(id+"F16.imprint","IMPRINT",FACE,{"disambiguationData":[TD([[makeQuery(id+"F16.imprint","IMPRINT",EDGE,{"derivedFrom":sQuery(id+"F16.wireOp",EDGE,"E87.MirrorCS")}),-1.0]])]});
            var Q1;
            {var subQ1=sQuery(id+"F16.wireOp",EDGE,"E79");Q1=makeQuery(id+"F16.imprint","IMPRINT",FACE,{"disambiguationData":[TD([[makeQuery(id+"F16.imprint","IMPRINT",EDGE,{"derivedFrom":subQ1}),-1.0]])]});}
            var Q2;
            Q2=makeQuery(id+"F2.opExtrude","CAP_FACE",FACE,{"disambiguationData":[OSD([sQuery(id+"F0.wireOp",EDGE,"E12"),sQuery(id+"F0.wireOp",EDGE,"E13"),sQuery(id+"F0.wireOp",EDGE,"E14"),sQuery(id+"F0.wireOp",EDGE,"E15"),sQuery(id+"F0.wireOp",EDGE,"E17.filletArc"),sQuery(id+"F0.wireOp",EDGE,"E18.filletArc"),sQuery(id+"F0.wireOp",EDGE,"E19.filletArc"),sQuery(id+"F0.wireOp",EDGE,"E20.filletArc"),sQuery(id+"F0.wireOp",EDGE,"E25.0"),sQuery(id+"F0.wireOp",EDGE,"E25.1"),sQuery(id+"F0.wireOp",EDGE,"E25.2"),sQuery(id+"F0.wireOp",EDGE,"E25.3"),sQuery(id+"F0.wireOp",EDGE,"E25.4"),sQuery(id+"F0.wireOp",EDGE,"E25.5"),sQuery(id+"F0.wireOp",EDGE,"E25.6"),sQuery(id+"F0.wireOp",EDGE,"E25.7")])],"isStart":false});
            extrude(context, id + "F17", {"entities" : qUnion([Q0, Q1]), "endBound" : BoundingType.UP_TO_SURFACE, "endBoundEntityFace" : qUnion([Q2]), "depth" : 25 * mm});
        }
    });
